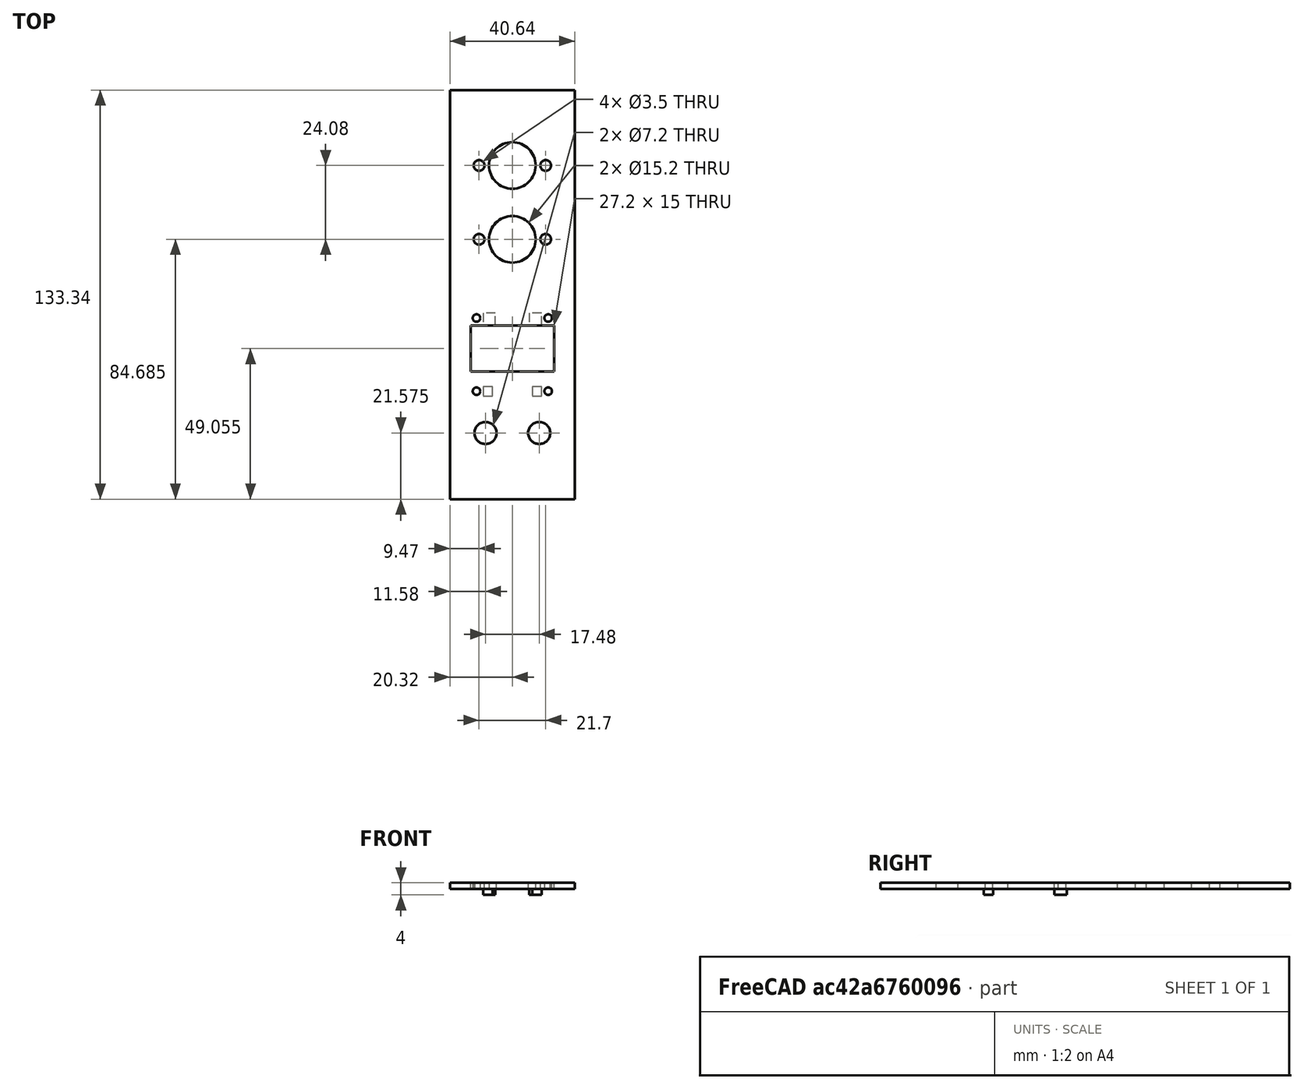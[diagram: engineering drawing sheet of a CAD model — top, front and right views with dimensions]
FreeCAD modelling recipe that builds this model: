
FCSTD DOCUMENT  (FreeCAD 0.17R13541 (Git))
Label: Cover Plate
License: All rights reserved
LicenseURL: http://en.wikipedia.org/wiki/All_rights_reserved
objects: Sketcher::SketchObject×2, PartDesign::Pad×2, Spreadsheet::Sheet×1, App::Part×1, PartDesign::Body×1, Mesh::Feature×1
note: 7 computed .brp shape members not serialized (recipe doc carries the construction recipe); baked Part::Feature solids carry a one-line shape summary decoded from their .brp

FEATURE [Spreadsheet::Sheet] Spreadsheet  label="D"
  cells = B2=U; C2(U)==44.450000000000003mm; B3=3U; C3(TU)==C2 * 3; B4=HP; C4(HP)==5.0800000000000001mm
FEATURE [App::Part] Part
  License = CC BY 3.0
  LicenseURL = http://creativecommons.org/licenses/by/3.0/
  Origin = -> Origin
FEATURE [Sketcher::SketchObject] Sketch
  MapMode = 5
  Support = -> [XY_Plane001]
  expr: Constraints[22] = 2.25 / 2 + 0.10000000000000001
  expr: Constraints[24] = 2.25 / 2 + 0.10000000000000001
  expr: Constraints[23] = 2.25 / 2 + 0.10000000000000001
  expr: Constraints[47] = 3.5 + 0.10000000000000001
  expr: Constraints[65] = 7.5 + 0.10000000000000001
  expr: Constraints[69] = 1.6499999999999999 + 0.10000000000000001
  expr: Constraints[46] = 3.5 + 0.10000000000000001
  expr: Constraints[67] = 1.6499999999999999 + 0.10000000000000001
  expr: Constraints[64] = 7.5 + 0.10000000000000001
  expr: Constraints[98] = 19mm / 2 + D.HP
  expr: Constraints[96] = 13mm / 2 + D.HP
  expr: Constraints[97] = 19mm + D.HP
  expr: Constraints[54] = 13mm / 2 + D.HP
  expr: Constraints[21] = 2.25 / 2 + 0.10000000000000001
  expr: Constraints[31] = 2.25 / 2 + 0.80000000000000004
  expr: Constraints[25] = 2.25 / 2 + 1
  expr: Constraints[30] = 2.25 / 2 + 0.90000000000000002
  expr: Constraints[32] = 2.25 / 2 + 0.80000000000000004
  expr: Constraints[95] = 13mm / 2 + D.HP
  expr: Constraints[9] = D.TU
  expr: Constraints[70] = 1.6499999999999999 + 0.10000000000000001
  expr: Constraints[68] = 1.6499999999999999 + 0.10000000000000001
  expr: Constraints[8] = 8 * D.HP
  sketch-geometry (36):
    g0: LineSegment StartX=-20.32 StartY=66.675 StartZ=0 EndX=20.32 EndY=66.675 EndZ=0
    g1: LineSegment StartX=20.32 StartY=66.675 StartZ=0 EndX=20.32 EndY=-66.675 EndZ=0
    g2: LineSegment StartX=20.32 StartY=-66.675 StartZ=0 EndX=-20.32 EndY=-66.675 EndZ=0
    g3: LineSegment StartX=-20.32 StartY=-66.675 StartZ=0 EndX=-20.32 EndY=66.675 EndZ=0
    g4: LineSegment [constr] StartX=-13.6 StartY=-5.515 StartZ=0 EndX=13.6 EndY=-5.515 EndZ=0
    g5: LineSegment [constr] StartX=13.6 StartY=-5.515 StartZ=0 EndX=13.6 EndY=-33.515 EndZ=0
    g6: LineSegment [constr] StartX=13.6 StartY=-33.515 StartZ=0 EndX=-13.6 EndY=-33.515 EndZ=0
    g7: LineSegment [constr] StartX=-13.6 StartY=-33.515 StartZ=0 EndX=-13.6 EndY=-5.515 EndZ=0
    g8: Circle CenterX=-11.675 CenterY=-7.64 CenterZ=0 NormalX=0 NormalY=0 NormalZ=1 AngleXU=0 Radius=1.225
    g9: Circle CenterX=11.675 CenterY=-7.64 CenterZ=0 NormalX=0 NormalY=0 NormalZ=1 AngleXU=0 Radius=1.225
    g10: Circle CenterX=11.675 CenterY=-31.49 CenterZ=0 NormalX=0 NormalY=0 NormalZ=1 AngleXU=0 Radius=1.225
    g11: Circle CenterX=-11.675 CenterY=-31.49 CenterZ=0 NormalX=0 NormalY=0 NormalZ=1 AngleXU=0 Radius=1.225
    g12: LineSegment StartX=-13.6 StartY=-10.115 StartZ=0 EndX=13.6 EndY=-10.115 EndZ=0
    g13: LineSegment StartX=13.6 StartY=-10.115 StartZ=0 EndX=13.6 EndY=-25.115 EndZ=0
    g14: LineSegment StartX=13.6 StartY=-25.115 StartZ=0 EndX=-13.6 EndY=-25.115 EndZ=0
    g15: LineSegment StartX=-13.6 StartY=-25.115 StartZ=0 EndX=-13.6 EndY=-10.115 EndZ=0
    g16: Circle CenterX=-8.74 CenterY=-45.095 CenterZ=0 NormalX=0 NormalY=0 NormalZ=1 AngleXU=0 Radius=3.6
    g17: Circle CenterX=8.74 CenterY=-45.095 CenterZ=0 NormalX=0 NormalY=0 NormalZ=1 AngleXU=0 Radius=3.6
    g18: Circle [constr] CenterX=8.74 CenterY=-45.095 CenterZ=0 NormalX=0 NormalY=0 NormalZ=1 AngleXU=0 Radius=6.5
    g19: Circle [constr] CenterX=-8.74 CenterY=-45.095 CenterZ=0 NormalX=0 NormalY=0 NormalZ=1 AngleXU=0 Radius=6.5
    g20: Circle CenterX=0 CenterY=18.015 CenterZ=0 NormalX=0 NormalY=0 NormalZ=1 AngleXU=0 Radius=7.6
    g21: Circle CenterX=0 CenterY=42.095 CenterZ=0 NormalX=0 NormalY=0 NormalZ=1 AngleXU=0 Radius=7.6
    g22: Circle CenterX=10.85 CenterY=42.095 CenterZ=0 NormalX=0 NormalY=0 NormalZ=1 AngleXU=0 Radius=1.75
    g23: Circle CenterX=-10.85 CenterY=42.095 CenterZ=0 NormalX=0 NormalY=0 NormalZ=1 AngleXU=0 Radius=1.75
    g24: Circle CenterX=-10.85 CenterY=18.015 CenterZ=0 NormalX=0 NormalY=0 NormalZ=1 AngleXU=0 Radius=1.75
    g25: Circle CenterX=10.85 CenterY=18.015 CenterZ=0 NormalX=0 NormalY=0 NormalZ=1 AngleXU=0 Radius=1.75
    g26: Circle [constr] CenterX=0 CenterY=18.015 CenterZ=0 NormalX=0 NormalY=0 NormalZ=1 AngleXU=0 Radius=9.5
    g27: Circle [constr] CenterX=10.85 CenterY=18.015 CenterZ=0 NormalX=0 NormalY=0 NormalZ=1 AngleXU=0 Radius=3.65
    g28: Circle [constr] CenterX=-10.85 CenterY=18.015 CenterZ=0 NormalX=0 NormalY=0 NormalZ=1 AngleXU=0 Radius=3.65
    g29: Circle [constr] CenterX=-10.85 CenterY=42.095 CenterZ=0 NormalX=0 NormalY=0 NormalZ=1 AngleXU=0 Radius=3.65
    g30: Circle [constr] CenterX=10.85 CenterY=42.095 CenterZ=0 NormalX=0 NormalY=0 NormalZ=1 AngleXU=0 Radius=3.65
    g31: Circle [constr] CenterX=0 CenterY=42.095 CenterZ=0 NormalX=0 NormalY=0 NormalZ=1 AngleXU=0 Radius=9.5
    g32: LineSegment [constr] StartX=-20.32 StartY=56.675 StartZ=0 EndX=20.32 EndY=56.675 EndZ=0
    g33: LineSegment StartX=20.32 StartY=56.675 StartZ=0 EndX=20.32 EndY=-56.675 EndZ=0
    g34: LineSegment [constr] StartX=20.32 StartY=-56.675 StartZ=0 EndX=-20.32 EndY=-56.675 EndZ=0
    g35: LineSegment StartX=-20.32 StartY=-56.675 StartZ=0 EndX=-20.32 EndY=56.675 EndZ=0
  constraints (99):
    c: Coincident(g0,g1)
    c: Coincident(g1,g2)
    c: Coincident(g2,g3)
    c: Coincident(g3,g0)
    c: Horizontal(g0)
    c: Horizontal(g2)
    c: Vertical(g1)
    c: Vertical(g3)
    c: Distance(g0) = 40.64
    c: Distance(g3) = 133.35
    c: Symmetric(g0,g1,g-1)
    c: Coincident(g4,g5)
    c: Coincident(g5,g6)
    c: Coincident(g6,g7)
    c: Coincident(g7,g4)
    c: Horizontal(g4)
    c: Horizontal(g6)
    c: Vertical(g5)
    c: Vertical(g7)
    c: Distance(g5) = 28
    c: Distance(g4) = 27.2
    c: Radius(g8) = 1.225
    c: Radius(g9) = 1.225
    c: Radius(g11) = 1.225
    c: Radius(g10) = 1.225
    c: Distance(g8,g4) = 2.125
    c: Horizontal(g8,g9)
    c: Horizontal(g11,g10)
    c: Vertical(g11,g8)
    c: Vertical(g9,g10)
    c: Distance(g11,g6) = 2.025
    c: Distance(g8,g7) = 1.925
    c: Distance(g9,g5) = 1.925
    c: Coincident(g12,g13)
    c: Coincident(g13,g14)
    c: Coincident(g14,g15)
    c: Coincident(g15,g12)
    c: Horizontal(g12)
    c: Horizontal(g14)
    c: Vertical(g13)
    c: Vertical(g15)
    c: PointOnObject(g12,g7)
    c: PointOnObject(g13,g5)
    c: Distance(g12,g4) = 4.6
    c: Distance(g12,g14) = 15
    c: Horizontal(g17,g16)
    c: Radius(g16) = 3.6
    c: Radius(g17) = 3.6
    c: Coincident(g18,g17)
    c: Coincident(g19,g16)
    c: Radius(g19) = 6.5
    c: Radius(g18) = 6.5
    c: Symmetric(g16,g17,g-2)
    c: Symmetric(g6,g5,g-2)
    c: Distance(g16,g3) = 11.58
    c: PointOnObject(g20,g-2)
    c: PointOnObject(g21,g-2)
    c: Horizontal(g23,g21)
    c: Horizontal(g21,g22)
    c: Horizontal(g24,g20)
    c: Horizontal(g20,g25)
    c: Vertical(g23,g24)
    c: Vertical(g22,g25)
    c: Symmetric(g23,g22,g-2)
    c: Radius(g21) = 7.6
    c: Radius(g20) = 7.6
    c: Distance(g23,g22) = 21.7
    c: Radius(g23) = 1.75
    c: Radius(g22) = 1.75
    c: Radius(g24) = 1.75
    c: Radius(g25) = 1.75
    c: Coincident(g26,g20)
    c: Radius(g26) = 9.5
    c: Coincident(g27,g25)
    c: Radius(g27) = 3.65
    c: Coincident(g28,g24)
    c: Coincident(g29,g23)
    c: Coincident(g30,g22)
    c: Radius(g28) = 3.65
    c: Radius(g29) = 3.65
    c: Radius(g30) = 3.65
    c: Coincident(g31,g21)
    c: Radius(g31) = 9.5
    c: Coincident(g32,g33)
    c: Coincident(g33,g34)
    c: Coincident(g34,g35)
    c: Coincident(g35,g32)
    c: Horizontal(g32)
    c: Horizontal(g34)
    c: Vertical(g33)
    c: Vertical(g35)
    c: PointOnObject(g32,g3)
    c: PointOnObject(g33,g1)
    c: Symmetric(g33,g32,g-1)
    c: Distance(g32,g0) = 10
    c: Distance(g16,g34) = 11.58
    c: DistanceY(g16,g6) = 11.58
    c: DistanceY(g20,g21) = 24.08
    c: Distance(g21,g32) = 14.58
FEATURE [PartDesign::Pad] Pad
  Length = 2
  Length2 = 100
  Profile = -> Sketch
  Type = 0
FEATURE [Sketcher::SketchObject] Sketch001
  MapMode = 5
  Placement = pos=(0,0,0) rot=(1,0,0;3.14159rad)
  Support = -> [Pad]
  sketch-geometry (24):
    g0: LineSegment StartX=-9.5 StartY=33 StartZ=0 EndX=-6.5 EndY=33 EndZ=0
    g1: LineSegment StartX=-6.5 StartY=33 StartZ=0 EndX=-6.5 EndY=30 EndZ=0
    g2: LineSegment StartX=-6.5 StartY=30 StartZ=0 EndX=-9.5 EndY=30 EndZ=0
    g3: LineSegment StartX=-9.5 StartY=30 StartZ=0 EndX=-9.5 EndY=33 EndZ=0
    g4: LineSegment StartX=6.5 StartY=33 StartZ=0 EndX=9.5 EndY=33 EndZ=0
    g5: LineSegment StartX=9.5 StartY=33 StartZ=0 EndX=9.5 EndY=30 EndZ=0
    g6: LineSegment StartX=9.5 StartY=30 StartZ=0 EndX=6.5 EndY=30 EndZ=0
    g7: LineSegment StartX=6.5 StartY=30 StartZ=0 EndX=6.5 EndY=33 EndZ=0
    g8: LineSegment StartX=-9.5 StartY=10 StartZ=0 EndX=-5.5 EndY=10 EndZ=0
    g9: LineSegment StartX=-5.5 StartY=10 StartZ=0 EndX=-5.5 EndY=6 EndZ=0
    g10: LineSegment StartX=-5.5 StartY=6 StartZ=0 EndX=-9.5 EndY=6 EndZ=0
    g11: LineSegment StartX=-9.5 StartY=6 StartZ=0 EndX=-9.5 EndY=10 EndZ=0
    g12: LineSegment StartX=5.5 StartY=10 StartZ=0 EndX=9.5 EndY=10 EndZ=0
    g13: LineSegment StartX=9.5 StartY=10 StartZ=0 EndX=9.5 EndY=6 EndZ=0
    g14: LineSegment StartX=9.5 StartY=6 StartZ=0 EndX=5.5 EndY=6 EndZ=0
    g15: LineSegment StartX=5.5 StartY=6 StartZ=0 EndX=5.5 EndY=10 EndZ=0
    g16: LineSegment [constr] StartX=-5 StartY=10 StartZ=0 EndX=5 EndY=10 EndZ=0
    g17: LineSegment [constr] StartX=5 StartY=10 StartZ=0 EndX=5 EndY=6 EndZ=0
    g18: LineSegment [constr] StartX=5 StartY=6 StartZ=0 EndX=-5 EndY=6 EndZ=0
    g19: LineSegment [constr] StartX=-5 StartY=6 StartZ=0 EndX=-5 EndY=10 EndZ=0
    g20: LineSegment [constr] StartX=-6 StartY=33 StartZ=0 EndX=6 EndY=33 EndZ=0
    g21: LineSegment [constr] StartX=6 StartY=33 StartZ=0 EndX=6 EndY=30 EndZ=0
    g22: LineSegment [constr] StartX=6 StartY=30 StartZ=0 EndX=-6 EndY=30 EndZ=0
    g23: LineSegment [constr] StartX=-6 StartY=30 StartZ=0 EndX=-6 EndY=33 EndZ=0
  constraints (69):
    c: Coincident(g0,g1)
    c: Coincident(g1,g2)
    c: Coincident(g2,g3)
    c: Coincident(g3,g0)
    c: Horizontal(g0)
    c: Horizontal(g2)
    c: Vertical(g1)
    c: Vertical(g3)
    c: Coincident(g4,g5)
    c: Coincident(g5,g6)
    c: Coincident(g6,g7)
    c: Coincident(g7,g4)
    c: Horizontal(g4)
    c: Horizontal(g6)
    c: Vertical(g5)
    c: Vertical(g7)
    c: Coincident(g8,g9)
    c: Coincident(g9,g10)
    c: Coincident(g10,g11)
    c: Coincident(g11,g8)
    c: Horizontal(g8)
    c: Horizontal(g10)
    c: Vertical(g9)
    c: Vertical(g11)
    c: Coincident(g12,g13)
    c: Coincident(g13,g14)
    c: Coincident(g14,g15)
    c: Coincident(g15,g12)
    c: Horizontal(g12)
    c: Horizontal(g14)
    c: Vertical(g13)
    c: Vertical(g15)
    c: Coincident(g16,g17)
    c: Coincident(g17,g18)
    c: Coincident(g18,g19)
    c: Coincident(g19,g16)
    c: Horizontal(g16)
    c: Horizontal(g18)
    c: Vertical(g17)
    c: Vertical(g19)
    c: Symmetric(g16,g16,g-2)
    c: Distance(g16,g16) = 10
    c: Coincident(g20,g21)
    c: Coincident(g21,g22)
    c: Coincident(g22,g23)
    c: Coincident(g23,g20)
    c: Horizontal(g20)
    c: Horizontal(g22)
    c: Vertical(g21)
    c: Vertical(g23)
    c: Distance(g21,g22) = 12
    c: Symmetric(g21,g22,g-2)
    c: DistanceX(g8,g16) = 0.5
    c: Symmetric(g8,g12,g-2)
    c: Distance(g8) = 4
    c: DistanceY(g-1,g8) = 10
    c: Distance(g8,g10) = 4
    c: Symmetric(g9,g14,g-2)
    c: Symmetric(g13,g10,g-2)
    c: Distance(g0) = 3
    c: Vertical(g8,g2)
    c: Distance(g1) = 3
    c: Symmetric(g4,g0,g-2)
    c: Symmetric(g5,g2,g-2)
    c: DistanceY(g-1,g2) = 30
    c: Horizontal(g22,g1)
    c: Horizontal(g20,g0)
    c: Horizontal(g16,g8)
    c: Horizontal(g18,g9)
FEATURE [PartDesign::Pad] Pad001
  BaseFeature = -> Pad
  Length = 2
  Length2 = 100
  Profile = -> Sketch001
  Type = 0
FEATURE [PartDesign::Body] Body
  Group = -> [Sketch,Pad,Sketch001,Pad001]
  Origin = -> Origin001
  Tip = -> Pad001
FEATURE [Mesh::Feature] Mesh  label="Body (Meshed)"
